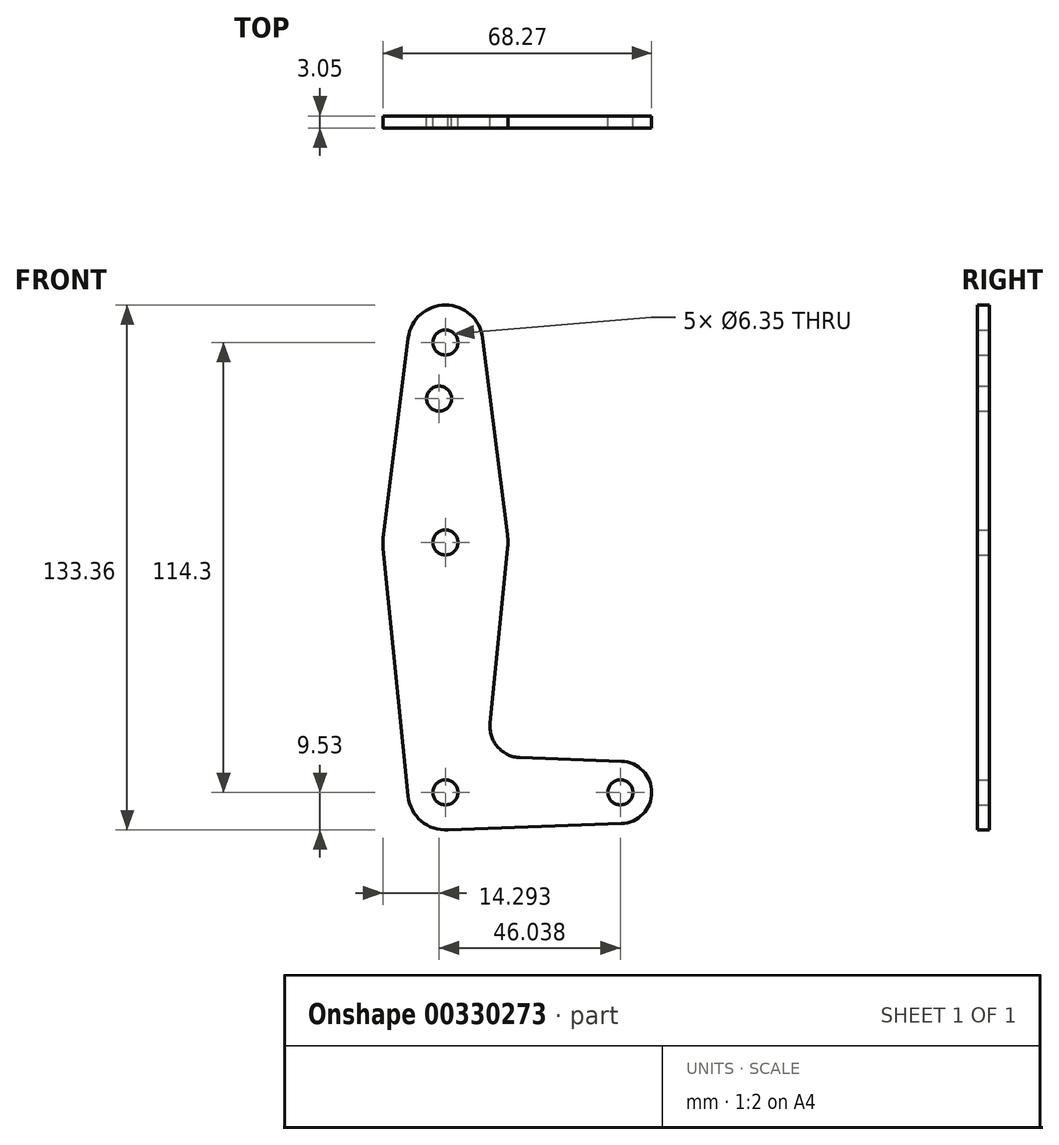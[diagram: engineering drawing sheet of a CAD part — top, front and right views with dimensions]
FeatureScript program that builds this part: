
annotation { "Feature Type Name" : "Feature", "Feature Type Description" : "" }
export const myFeature = defineFeature(function(context is Context, id is Id, definition is map)
    precondition{}
    {
        {
            var Q0;
            Q0=qCreatedBy(makeId("Front.planeOp"),FACE);
            var sketch = newSketch(context, id + "F0", { "sketchPlane" : qUnion([Q0])});
            skLineSegment(sketch, "E0", {"start": v(0, 114.3) * mm, "end": v(0, 0) * mm, "construction": true});
            skLineSegment(sketch, "E1", {"start": v(0, 0) * mm, "end": v(44.45, 0) * mm, "construction": true});
            skCircle(sketch, "E2", {"center": v(0, 114.3) * mm, "radius": 9.53 * mm});
            skCircle(sketch, "E3", {"center": v(0, 0) * mm, "radius": 9.53 * mm});
            skCircle(sketch, "E4", {"center": v(44.45, 0) * mm, "radius": 7.94 * mm});
            skCircle(sketch, "E5", {"center": v(0, 63.5) * mm, "radius": 15.88 * mm});
            skLineSegment(sketch, "E6", {"start": v(-9.45, 115.5) * mm, "end": v(-15.75, 65.48) * mm});
            skLineSegment(sketch, "E7", {"start": v(9.45, 115.5) * mm, "end": v(15.75, 65.48) * mm});
            skLineSegment(sketch, "E8", {"start": v(15.8, 61.91) * mm, "end": v(11.34, 17.59) * mm});
            skLineSegment(sketch, "E9", {"start": v(18.97, 8.85) * mm, "end": v(44.73, 7.93) * mm});
            skLineSegment(sketch, "E10", {"start": v(0, -9.53) * mm, "end": v(44.73, -7.93) * mm});
            skLineSegment(sketch, "E11", {"start": v(-15.8, 61.91) * mm, "end": v(-9.48, -0.95) * mm});
            skCircle(sketch, "E12", {"center": v(0, 114.3) * mm, "radius": 3.18 * mm});
            skCircle(sketch, "E13", {"center": v(-1.59, 100.03) * mm, "radius": 3.18 * mm});
            skCircle(sketch, "E14", {"center": v(0, 63.5) * mm, "radius": 3.18 * mm});
            skCircle(sketch, "E15", {"center": v(0, 0) * mm, "radius": 3.18 * mm});
            skCircle(sketch, "E16", {"center": v(44.45, 0) * mm, "radius": 3.18 * mm});
            skArc(sketch, "E17.filletArc", {"start": v(11.34, 17.59) * mm, "mid": v(13.26, 11.57) * mm, "end": v(18.97, 8.85) * mm});
            skSolve(sketch);
        }
        {
            var Q0;
            Q0 = qSketchRegion(id + "F0", true);
            extrude(context, id + "F1", {"entities" : qUnion([Q0]), "depth" : 3.05 * mm});
        }
    });
